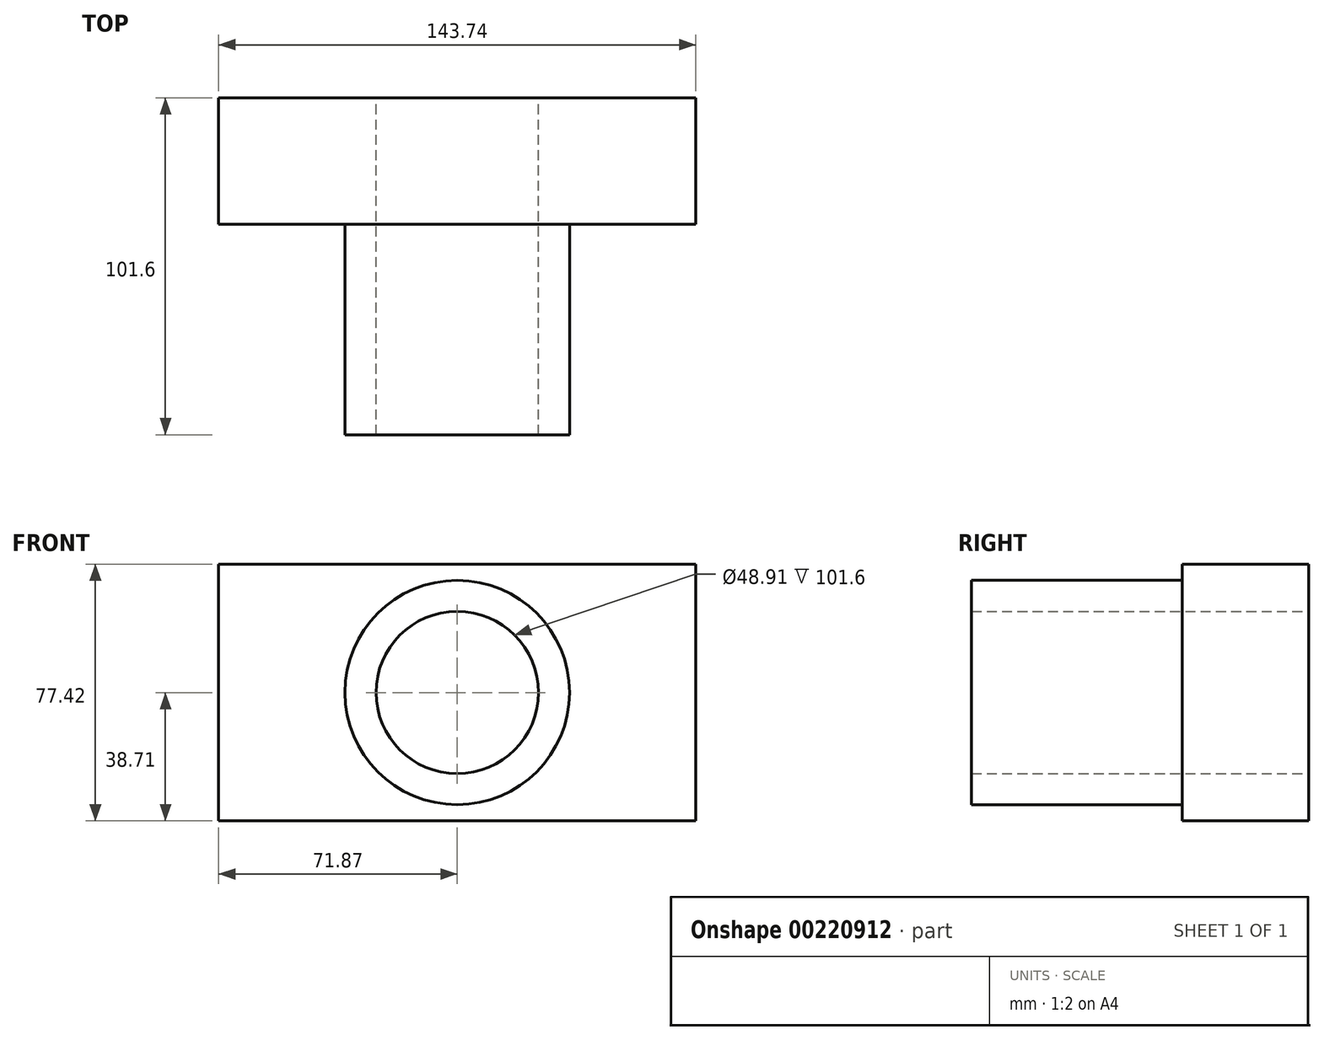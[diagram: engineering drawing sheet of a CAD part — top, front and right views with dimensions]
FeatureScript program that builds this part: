
annotation { "Feature Type Name" : "Feature", "Feature Type Description" : "" }
export const myFeature = defineFeature(function(context is Context, id is Id, definition is map)
    precondition{}
    {
        {
            var Q0;
            Q0=qCreatedBy(makeId("Front.planeOp"),FACE);
            var sketch = newSketch(context, id + "F0", { "sketchPlane" : qUnion([Q0])});
            skLineSegment(sketch, "E0.bottom", {"start": v(71.87, 38.71) * mm, "end": v(-71.87, 38.71) * mm});
            skLineSegment(sketch, "E0.top", {"start": v(71.87, -38.71) * mm, "end": v(-71.87, -38.71) * mm});
            skLineSegment(sketch, "E0.left", {"start": v(71.87, 38.71) * mm, "end": v(71.87, -38.71) * mm});
            skLineSegment(sketch, "E0.right", {"start": v(-71.87, 38.71) * mm, "end": v(-71.87, -38.71) * mm});
            skPoint(sketch, "E0.middle", {"position": v(0, 0) * mm});
            skCircle(sketch, "E1", {"center": v(0, 0) * mm, "radius": 33.82 * mm});
            skCircle(sketch, "E2", {"center": v(0, 0) * mm, "radius": 24.46 * mm});
            skSolve(sketch);
        }
        {
            var Q0;
            Q0=makeQuery(id+"F0.imprint","IMPRINT",FACE,{"disambiguationData":[TD([[makeQuery(id+"F0.imprint","IMPRINT",EDGE,{"derivedFrom":sQuery(id+"F0.wireOp",EDGE,"E1")}),1.0]])]});
            extrude(context, id + "F1", {"entities" : qUnion([Q0]), "depth" : 101.6 * mm});
        }
        {
            var Q0;
            Q0=makeQuery(id+"F0.imprint","IMPRINT",FACE,{"disambiguationData":[TD([[makeQuery(id+"F0.imprint","IMPRINT",EDGE,{"derivedFrom":sQuery(id+"F0.wireOp",EDGE,"E0.bottom")}),1.0]])]});
            extrude(context, id + "F2", {"entities" : qUnion([Q0]), "operationType" : NewBodyOperationType.ADD, "depth" : 38.1 * mm});
        }
    });
